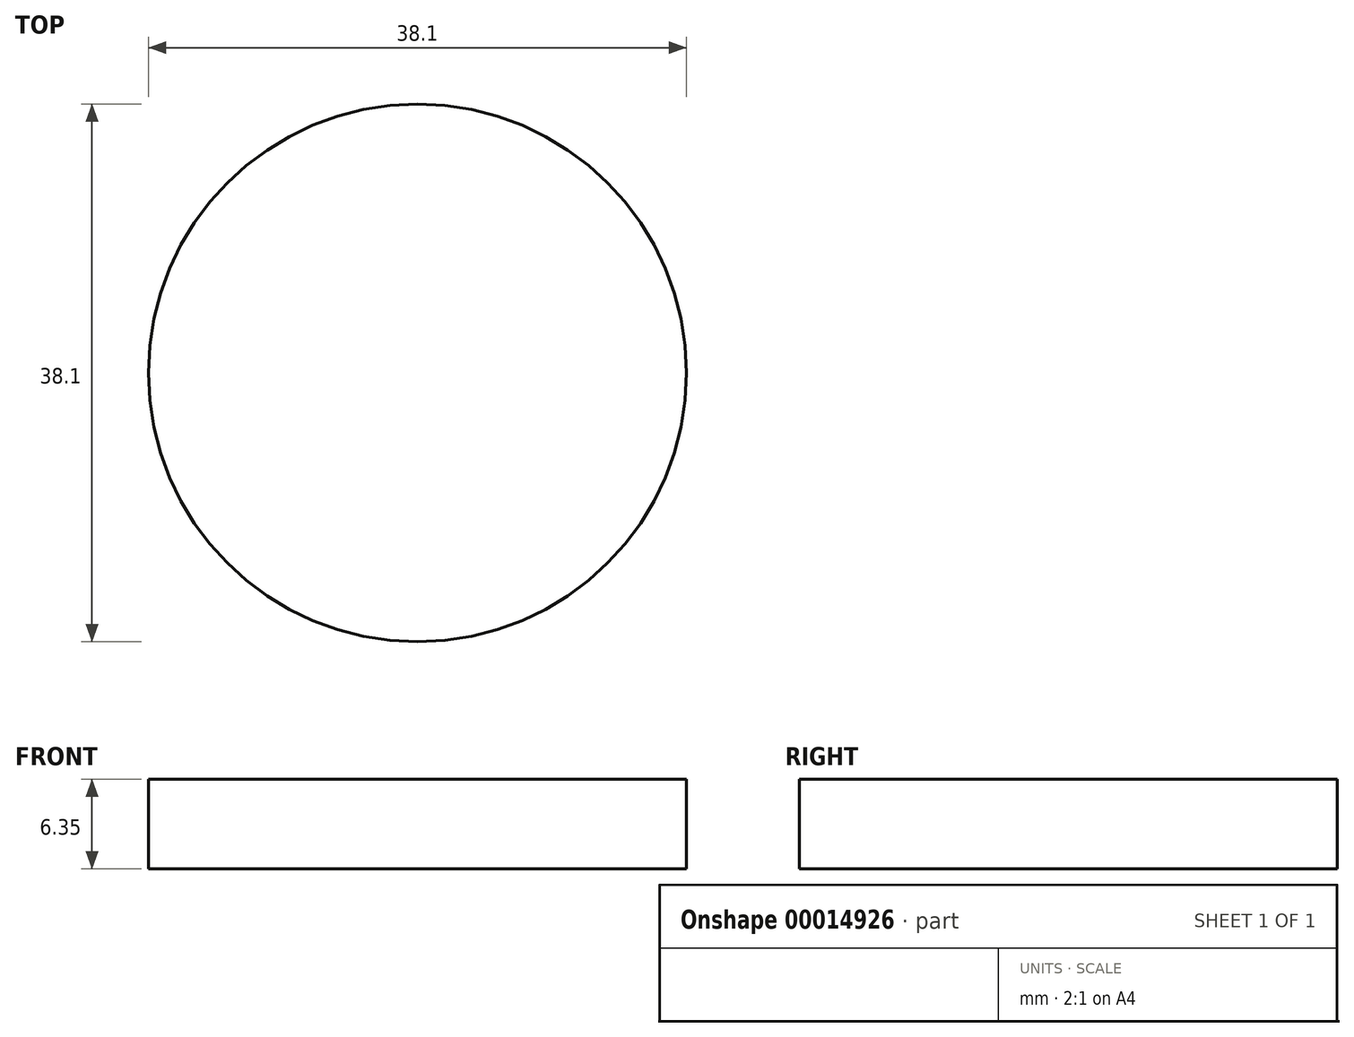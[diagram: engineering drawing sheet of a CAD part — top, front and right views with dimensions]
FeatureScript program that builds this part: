
annotation { "Feature Type Name" : "Feature", "Feature Type Description" : "" }
export const myFeature = defineFeature(function(context is Context, id is Id, definition is map)
    precondition{}
    {
        {
            var Q0;
            Q0=qCreatedBy(makeId("Top.planeOp"),FACE);
            var sketch = newSketch(context, id + "F0", { "sketchPlane" : qUnion([Q0])});
            skCircle(sketch, "E0", {"center": v(-49.27, 29.42) * mm, "radius": 19.05 * mm});
            skSolve(sketch);
        }
        {
            var Q0;
            Q0=makeQuery(id+"F0.imprint","IMPRINT",FACE,{"disambiguationData":[TD([[makeQuery(id+"F0.imprint","IMPRINT",EDGE,{"derivedFrom":sQuery(id+"F0.wireOp",EDGE,"E0")}),1.0]])]});
            extrude(context, id + "F1", {"entities" : qUnion([Q0]), "depth" : 6.35 * mm});
        }
    });
